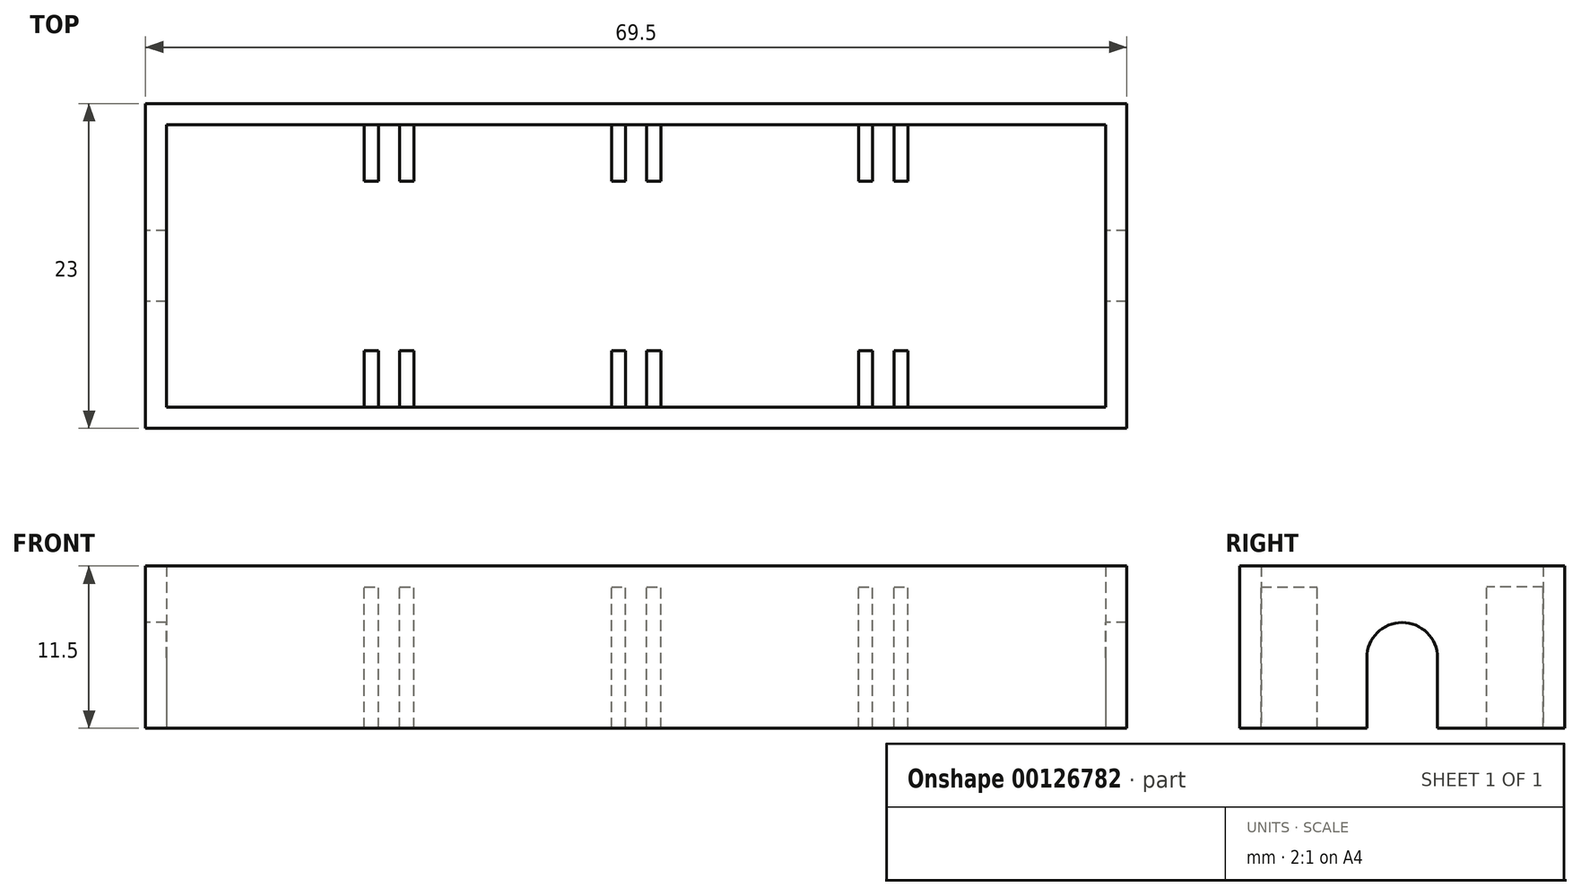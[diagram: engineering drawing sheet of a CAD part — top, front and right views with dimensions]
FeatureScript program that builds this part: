
annotation { "Feature Type Name" : "Feature", "Feature Type Description" : "" }
export const myFeature = defineFeature(function(context is Context, id is Id, definition is map)
    precondition{}
    {
        {
            var Q0;
            Q0=qCreatedBy(makeId("Top.planeOp"),FACE);
            var sketch = newSketch(context, id + "F0", { "sketchPlane" : qUnion([Q0])});
            skLineSegment(sketch, "E0.bottom", {"start": v(-29.8, 7) * mm, "end": v(-15.8, 7) * mm});
            skLineSegment(sketch, "E0.top", {"start": v(-29.8, -13) * mm, "end": v(-15.8, -13) * mm});
            skLineSegment(sketch, "E0.left", {"start": v(-29.8, 7) * mm, "end": v(-29.8, -13) * mm});
            skLineSegment(sketch, "E0.right", {"start": v(36.7, 7) * mm, "end": v(36.7, -13) * mm});
            skLineSegment(sketch, "E1.top", {"start": v(-15.8, 3) * mm, "end": v(-14.8, 3) * mm});
            skLineSegment(sketch, "E1.left", {"start": v(-15.8, 7) * mm, "end": v(-15.8, 3) * mm});
            skLineSegment(sketch, "E1.right", {"start": v(-14.8, 7) * mm, "end": v(-14.8, 3) * mm});
            skLineSegment(sketch, "E2.top", {"start": v(-13.3, 3) * mm, "end": v(-12.3, 3) * mm});
            skLineSegment(sketch, "E2.left", {"start": v(-13.3, 7) * mm, "end": v(-13.3, 3) * mm});
            skLineSegment(sketch, "E2.right", {"start": v(-12.3, 7) * mm, "end": v(-12.3, 3) * mm});
            skLineSegment(sketch, "E3.top", {"start": v(4.2, 3) * mm, "end": v(5.2, 3) * mm});
            skLineSegment(sketch, "E3.left", {"start": v(4.2, 7) * mm, "end": v(4.2, 3) * mm});
            skLineSegment(sketch, "E3.right", {"start": v(5.2, 7) * mm, "end": v(5.2, 3) * mm});
            skLineSegment(sketch, "E4.top", {"start": v(19.2, 3) * mm, "end": v(20.2, 3) * mm});
            skLineSegment(sketch, "E4.left", {"start": v(19.2, 7) * mm, "end": v(19.2, 3) * mm});
            skLineSegment(sketch, "E4.right", {"start": v(20.2, 7) * mm, "end": v(20.2, 3) * mm});
            skLineSegment(sketch, "E5.top", {"start": v(21.7, 3) * mm, "end": v(22.7, 3) * mm});
            skLineSegment(sketch, "E5.left", {"start": v(21.7, 7) * mm, "end": v(21.7, 3) * mm});
            skLineSegment(sketch, "E5.right", {"start": v(22.7, 7) * mm, "end": v(22.7, 3) * mm});
            skLineSegment(sketch, "E6.top", {"start": v(-15.8, -9) * mm, "end": v(-14.8, -9) * mm});
            skLineSegment(sketch, "E6.left", {"start": v(-15.8, -13) * mm, "end": v(-15.8, -9) * mm});
            skLineSegment(sketch, "E6.right", {"start": v(-14.8, -13) * mm, "end": v(-14.8, -9) * mm});
            skLineSegment(sketch, "E7.top", {"start": v(-13.3, -9) * mm, "end": v(-12.3, -9) * mm});
            skLineSegment(sketch, "E7.left", {"start": v(-13.3, -13) * mm, "end": v(-13.3, -9) * mm});
            skLineSegment(sketch, "E7.right", {"start": v(-12.3, -13) * mm, "end": v(-12.3, -9) * mm});
            skLineSegment(sketch, "E8.top", {"start": v(1.7, -9) * mm, "end": v(2.7, -9) * mm});
            skLineSegment(sketch, "E8.left", {"start": v(1.7, -13) * mm, "end": v(1.7, -9) * mm});
            skLineSegment(sketch, "E8.right", {"start": v(2.7, -13) * mm, "end": v(2.7, -9) * mm});
            skLineSegment(sketch, "E9.top", {"start": v(4.2, -9) * mm, "end": v(5.2, -9) * mm});
            skLineSegment(sketch, "E9.left", {"start": v(4.2, -13) * mm, "end": v(4.2, -9) * mm});
            skLineSegment(sketch, "E9.right", {"start": v(5.2, -13) * mm, "end": v(5.2, -9) * mm});
            skLineSegment(sketch, "E10.top", {"start": v(19.2, -9) * mm, "end": v(20.2, -9) * mm});
            skLineSegment(sketch, "E10.left", {"start": v(19.2, -13) * mm, "end": v(19.2, -9) * mm});
            skLineSegment(sketch, "E10.right", {"start": v(20.2, -13) * mm, "end": v(20.2, -9) * mm});
            skLineSegment(sketch, "E11.top", {"start": v(21.7, -9) * mm, "end": v(22.7, -9) * mm});
            skLineSegment(sketch, "E11.left", {"start": v(21.7, -13) * mm, "end": v(21.7, -9) * mm});
            skLineSegment(sketch, "E11.right", {"start": v(22.7, -13) * mm, "end": v(22.7, -9) * mm});
            skLineSegment(sketch, "E12.top", {"start": v(1.7, 3) * mm, "end": v(2.7, 3) * mm});
            skLineSegment(sketch, "E12.left", {"start": v(1.7, 7) * mm, "end": v(1.7, 3) * mm});
            skLineSegment(sketch, "E12.right", {"start": v(2.7, 7) * mm, "end": v(2.7, 3) * mm});
            skLineSegment(sketch, "E13.trimOffspring", {"start": v(-14.8, 7) * mm, "end": v(-13.3, 7) * mm});
            skLineSegment(sketch, "E14.trimOffspring", {"start": v(-12.3, 7) * mm, "end": v(1.7, 7) * mm});
            skLineSegment(sketch, "E15.trimOffspring", {"start": v(2.7, 7) * mm, "end": v(4.2, 7) * mm});
            skLineSegment(sketch, "E16.trimOffspring", {"start": v(5.2, 7) * mm, "end": v(19.2, 7) * mm});
            skLineSegment(sketch, "E17.trimOffspring", {"start": v(-14.8, -13) * mm, "end": v(-13.3, -13) * mm});
            skLineSegment(sketch, "E18.trimOffspring", {"start": v(-12.3, -13) * mm, "end": v(1.7, -13) * mm});
            skLineSegment(sketch, "E19.trimOffspring", {"start": v(2.7, -13) * mm, "end": v(4.2, -13) * mm});
            skLineSegment(sketch, "E20.trimOffspring", {"start": v(5.2, -13) * mm, "end": v(19.2, -13) * mm});
            skLineSegment(sketch, "E21.trimOffspring", {"start": v(20.2, -13) * mm, "end": v(21.7, -13) * mm});
            skLineSegment(sketch, "E22.trimOffspring", {"start": v(22.7, -13) * mm, "end": v(36.7, -13) * mm});
            skLineSegment(sketch, "E23.trimOffspring", {"start": v(20.2, 7) * mm, "end": v(21.7, 7) * mm});
            skLineSegment(sketch, "E24.trimOffspring", {"start": v(22.7, 7) * mm, "end": v(36.7, 7) * mm});
            skLineSegment(sketch, "E25", {"start": v(-29.8, -3) * mm, "end": v(37.18, -3) * mm, "construction": true});
            skLineSegment(sketch, "E26", {"start": v(-22.8, 7) * mm, "end": v(-22.8, -26.1) * mm, "construction": true});
            skLineSegment(sketch, "E27", {"start": v(-5.3, 7) * mm, "end": v(-5.3, -26.98) * mm, "construction": true});
            skLineSegment(sketch, "E28", {"start": v(12.2, 7) * mm, "end": v(12.2, -27.86) * mm, "construction": true});
            skLineSegment(sketch, "E29", {"start": v(29.7, 7) * mm, "end": v(29.7, -23.35) * mm, "construction": true});
            skCircle(sketch, "E30", {"center": v(-22.8, -3) * mm, "radius": 5.75 * mm, "construction": true});
            skCircle(sketch, "E31", {"center": v(-5.3, -3) * mm, "radius": 5.75 * mm, "construction": true});
            skCircle(sketch, "E32", {"center": v(12.2, -3) * mm, "radius": 5.75 * mm, "construction": true});
            skCircle(sketch, "E33", {"center": v(29.7, -3) * mm, "radius": 5.75 * mm, "construction": true});
            skLineSegment(sketch, "E34.bottom", {"start": v(-31.3, 8.5) * mm, "end": v(38.2, 8.5) * mm});
            skLineSegment(sketch, "E34.top", {"start": v(-31.3, -14.5) * mm, "end": v(38.2, -14.5) * mm});
            skLineSegment(sketch, "E34.left", {"start": v(-31.3, 8.5) * mm, "end": v(-31.3, -14.5) * mm});
            skLineSegment(sketch, "E34.right", {"start": v(38.2, 8.5) * mm, "end": v(38.2, -14.5) * mm});
            skLineSegment(sketch, "E35", {"start": v(-15.8, 7) * mm, "end": v(-14.8, 7) * mm});
            skLineSegment(sketch, "E36", {"start": v(-13.3, 7) * mm, "end": v(-12.3, 7) * mm});
            skLineSegment(sketch, "E37", {"start": v(1.7, 7) * mm, "end": v(2.7, 7) * mm});
            skLineSegment(sketch, "E38", {"start": v(4.2, 7) * mm, "end": v(5.2, 7) * mm});
            skLineSegment(sketch, "E39", {"start": v(19.2, 7) * mm, "end": v(20.2, 7) * mm});
            skLineSegment(sketch, "E40", {"start": v(21.7, 7) * mm, "end": v(22.7, 7) * mm});
            skLineSegment(sketch, "E41", {"start": v(-15.8, -13) * mm, "end": v(-14.8, -13) * mm});
            skLineSegment(sketch, "E42", {"start": v(-13.3, -13) * mm, "end": v(-12.3, -13) * mm});
            skLineSegment(sketch, "E43", {"start": v(1.7, -13) * mm, "end": v(2.7, -13) * mm});
            skLineSegment(sketch, "E44", {"start": v(4.2, -13) * mm, "end": v(5.2, -13) * mm});
            skLineSegment(sketch, "E45", {"start": v(19.2, -13) * mm, "end": v(20.2, -13) * mm});
            skLineSegment(sketch, "E46", {"start": v(21.7, -13) * mm, "end": v(22.7, -13) * mm});
            skSolve(sketch);
        }
        {
            var Q0;
            Q0=makeQuery(id+"F0.imprint","IMPRINT",FACE,{"disambiguationData":[TD([[makeQuery(id+"F0.imprint","IMPRINT",EDGE,{"derivedFrom":sQuery(id+"F0.wireOp",EDGE,"E0.bottom")}),1.0]])]});
            extrude(context, id + "F1", {"entities" : qUnion([Q0]), "depth" : 1.5 * mm});
        }
        {
            var Q0;
            Q0=makeQuery(id+"F0.imprint","IMPRINT",FACE,{"disambiguationData":[TD([[makeQuery(id+"F0.imprint","IMPRINT",EDGE,{"derivedFrom":sQuery(id+"F0.wireOp",EDGE,"E0.bottom")}),1.0]])]});
            var Q1;
            Q1=makeQuery(id+"F0.imprint","IMPRINT",FACE,{"disambiguationData":[TD([[makeQuery(id+"F0.imprint","IMPRINT",EDGE,{"derivedFrom":sQuery(id+"F0.wireOp",EDGE,"E6.top")}),-1.0]])]});
            var Q2;
            Q2=makeQuery(id+"F0.imprint","IMPRINT",FACE,{"disambiguationData":[TD([[makeQuery(id+"F0.imprint","IMPRINT",EDGE,{"derivedFrom":sQuery(id+"F0.wireOp",EDGE,"E7.top")}),-1.0]])]});
            var Q3;
            Q3=makeQuery(id+"F0.imprint","IMPRINT",FACE,{"disambiguationData":[TD([[makeQuery(id+"F0.imprint","IMPRINT",EDGE,{"derivedFrom":sQuery(id+"F0.wireOp",EDGE,"E8.top")}),-1.0]])]});
            var Q4;
            Q4=makeQuery(id+"F0.imprint","IMPRINT",FACE,{"disambiguationData":[TD([[makeQuery(id+"F0.imprint","IMPRINT",EDGE,{"derivedFrom":sQuery(id+"F0.wireOp",EDGE,"E9.top")}),-1.0]])]});
            var Q5;
            Q5=makeQuery(id+"F0.imprint","IMPRINT",FACE,{"disambiguationData":[TD([[makeQuery(id+"F0.imprint","IMPRINT",EDGE,{"derivedFrom":sQuery(id+"F0.wireOp",EDGE,"E10.top")}),-1.0]])]});
            var Q6;
            Q6=makeQuery(id+"F0.imprint","IMPRINT",FACE,{"disambiguationData":[TD([[makeQuery(id+"F0.imprint","IMPRINT",EDGE,{"derivedFrom":sQuery(id+"F0.wireOp",EDGE,"E11.top")}),-1.0]])]});
            var Q7;
            Q7=makeQuery(id+"F0.imprint","IMPRINT",FACE,{"disambiguationData":[TD([[makeQuery(id+"F0.imprint","IMPRINT",EDGE,{"derivedFrom":sQuery(id+"F0.wireOp",EDGE,"E5.top")}),1.0]])]});
            var Q8;
            Q8=makeQuery(id+"F0.imprint","IMPRINT",FACE,{"disambiguationData":[TD([[makeQuery(id+"F0.imprint","IMPRINT",EDGE,{"derivedFrom":sQuery(id+"F0.wireOp",EDGE,"E4.top")}),1.0]])]});
            var Q9;
            Q9=makeQuery(id+"F0.imprint","IMPRINT",FACE,{"disambiguationData":[TD([[makeQuery(id+"F0.imprint","IMPRINT",EDGE,{"derivedFrom":sQuery(id+"F0.wireOp",EDGE,"E3.top")}),1.0]])]});
            var Q10;
            Q10=makeQuery(id+"F0.imprint","IMPRINT",FACE,{"disambiguationData":[TD([[makeQuery(id+"F0.imprint","IMPRINT",EDGE,{"derivedFrom":sQuery(id+"F0.wireOp",EDGE,"E12.top")}),1.0]])]});
            var Q11;
            Q11=makeQuery(id+"F0.imprint","IMPRINT",FACE,{"disambiguationData":[TD([[makeQuery(id+"F0.imprint","IMPRINT",EDGE,{"derivedFrom":sQuery(id+"F0.wireOp",EDGE,"E2.top")}),1.0]])]});
            var Q12;
            Q12=makeQuery(id+"F0.imprint","IMPRINT",FACE,{"disambiguationData":[TD([[makeQuery(id+"F0.imprint","IMPRINT",EDGE,{"derivedFrom":sQuery(id+"F0.wireOp",EDGE,"E1.top")}),1.0]])]});
            extrude(context, id + "F2", {"entities" : qUnion([Q0, Q1, Q2, Q3, Q4, Q5, Q6, Q7, Q8, Q9, Q10, Q11, Q12]), "operationType" : NewBodyOperationType.ADD, "oppositeDirection" : true, "depth" : 10 * mm});
        }
        {
            var Q0;
            {var subQ0=sQuery(id+"F0.wireOp",EDGE,"E34.left");Q0=makeQuery(id+"F2.boolean.opBoolean","MERGE",FACE,{"derivedFrom":[makeQuery(id+"F1.opExtrude","SWEPT_FACE",FACE,{"disambiguationData":[OSD([subQ0])]}),makeQuery(id+"F2.opExtrude","SWEPT_FACE",FACE,{"disambiguationData":[OSD([subQ0])]})]});}
            var sketch = newSketch(context, id + "F3", { "sketchPlane" : qUnion([Q0])});
            skLineSegment(sketch, "E47", {"start": v(0.5, -10) * mm, "end": v(0.5, -5) * mm});
            skLineSegment(sketch, "E48", {"start": v(5.5, -10) * mm, "end": v(5.5, -5) * mm});
            skArc(sketch, "E49", {"start": v(5.5, -5) * mm, "mid": v(3, -2.5) * mm, "end": v(0.5, -5) * mm});
            skSolve(sketch);
        }
        {
            var Q0;
            {var subQ0=sQuery(id+"F3.wireOp",EDGE,"E47");Q0=makeQuery(id+"F3.imprint","IMPRINT",FACE,{"disambiguationData":[TD([[makeQuery(id+"F3.imprint","IMPRINT",EDGE,{"derivedFrom":subQ0}),-1.0]])]});}
            extrude(context, id + "F4", {"entities" : qUnion([Q0]), "operationType" : NewBodyOperationType.REMOVE, "endBound" : BoundingType.THROUGH_ALL, "oppositeDirection" : true, "depth" : 25 * mm});
        }
    });
